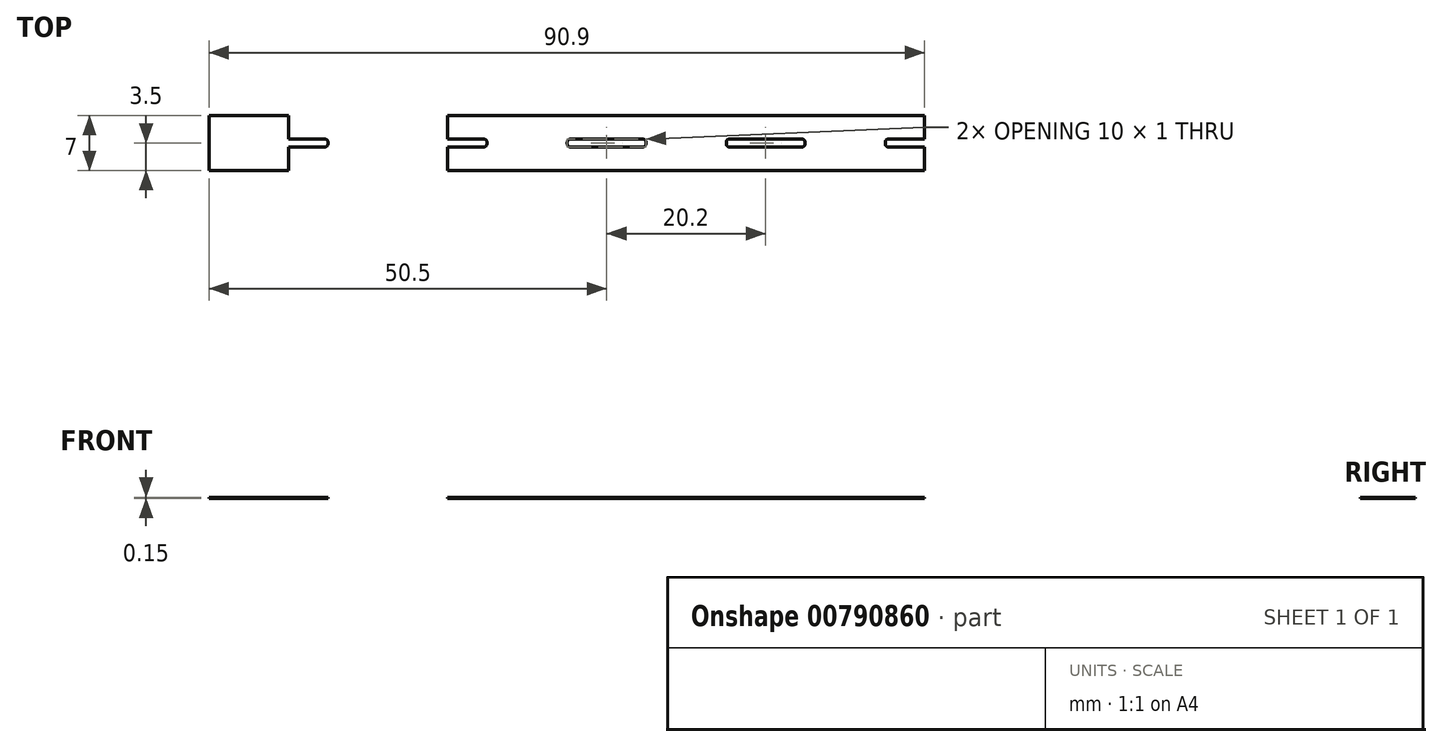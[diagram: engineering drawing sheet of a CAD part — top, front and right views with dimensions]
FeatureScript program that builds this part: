
annotation { "Feature Type Name" : "Feature", "Feature Type Description" : "" }
export const myFeature = defineFeature(function(context is Context, id is Id, definition is map)
    precondition{}
    {
        {
            var Q0;
            Q0=qCreatedBy(makeId("Top.planeOp"),FACE);
            var sketch = newSketch(context, id + "F0", { "sketchPlane" : qUnion([Q0])});
            skPoint(sketch, "E0.middle", {"position": v(0, 0) * mm});
            skLineSegment(sketch, "E1.bottom", {"start": v(-5.5, -0.5) * mm, "end": v(-10.1, -0.5) * mm});
            skLineSegment(sketch, "E1.top", {"start": v(-5.5, 0.5) * mm, "end": v(-10.1, 0.5) * mm});
            skLineSegment(sketch, "E1.left", {"start": v(-5.1, -0.1) * mm, "end": v(-5.1, 0.1) * mm});
            skLineSegment(sketch, "E1.right", {"start": v(-15.1, -0.1) * mm, "end": v(-15.1, 0.1) * mm});
            skPoint(sketch, "E1.middle", {"position": v(-10.1, 0) * mm});
            skPoint(sketch, "E2.visualSharp", {"position": v(-5.1, 0.5) * mm});
            skArc(sketch, "E2.filletArc", {"start": v(-5.1, 0.1) * mm, "mid": v(-5.22, 0.38) * mm, "end": v(-5.5, 0.5) * mm});
            skPoint(sketch, "E3.visualSharp", {"position": v(-5.1, -0.5) * mm});
            skArc(sketch, "E3.filletArc", {"start": v(-5.5, -0.5) * mm, "mid": v(-5.22, -0.38) * mm, "end": v(-5.1, -0.1) * mm});
            skPoint(sketch, "E4.visualSharp", {"position": v(-15.1, 0.5) * mm});
            skArc(sketch, "E4.filletArc", {"start": v(-14.7, 0.5) * mm, "mid": v(-14.98, 0.38) * mm, "end": v(-15.1, 0.1) * mm});
            skPoint(sketch, "E5.visualSharp", {"position": v(-15.1, -0.5) * mm});
            skArc(sketch, "E5.filletArc", {"start": v(-15.1, -0.1) * mm, "mid": v(-14.98, -0.38) * mm, "end": v(-14.7, -0.5) * mm});
            skLineSegment(sketch, "E6", {"start": v(0, 3.5) * mm, "end": v(-10.1, 3.5) * mm});
            skPoint(sketch, "E6.endSnap0", {"position": v(-10.1, 0.5) * mm});
            skLineSegment(sketch, "E7", {"start": v(-10.1, 3.5) * mm, "end": v(-10.1, 0.5) * mm});
            skLineSegment(sketch, "E8.MirrorCS", {"start": v(0, -3.5) * mm, "end": v(-10.1, -3.5) * mm});
            skLineSegment(sketch, "E9.MirrorCS", {"start": v(-10.1, -3.5) * mm, "end": v(-10.1, -0.5) * mm});
            skLineSegment(sketch, "E10.MirrorCS", {"start": v(0, 3.5) * mm, "end": v(10.1, 3.5) * mm});
            skLineSegment(sketch, "E11.MirrorCS", {"start": v(0, -3.5) * mm, "end": v(10.1, -3.5) * mm});
            skLineSegment(sketch, "E12.MirrorCS", {"start": v(5.1, -0.1) * mm, "end": v(5.1, 0.1) * mm});
            skArc(sketch, "E13.MirrorCS", {"start": v(5.1, 0.1) * mm, "mid": v(5.22, 0.38) * mm, "end": v(5.5, 0.5) * mm});
            skArc(sketch, "E14.MirrorCS", {"start": v(15.1, -0.1) * mm, "mid": v(14.98, -0.38) * mm, "end": v(14.7, -0.5) * mm});
            skLineSegment(sketch, "E15.MirrorCS", {"start": v(15.1, -0.1) * mm, "end": v(15.1, 0.1) * mm});
            skArc(sketch, "E16.MirrorCS", {"start": v(14.7, 0.5) * mm, "mid": v(14.98, 0.38) * mm, "end": v(15.1, 0.1) * mm});
            skArc(sketch, "E17.MirrorCS", {"start": v(5.5, -0.5) * mm, "mid": v(5.22, -0.38) * mm, "end": v(5.1, -0.1) * mm});
            skPoint(sketch, "E18.MirrorP", {"position": v(15.1, 0.5) * mm});
            skLineSegment(sketch, "E19.MirrorCS", {"start": v(5.5, 0.5) * mm, "end": v(14.7, 0.5) * mm});
            skLineSegment(sketch, "E20.MirrorCS", {"start": v(5.5, -0.5) * mm, "end": v(14.7, -0.5) * mm});
            skPoint(sketch, "E21.MirrorP", {"position": v(10.1, 0.5) * mm});
            skPoint(sketch, "E22.MirrorP", {"position": v(5.1, 0.5) * mm});
            skPoint(sketch, "E23.MirrorP", {"position": v(15.1, -0.5) * mm});
            skPoint(sketch, "E24.MirrorP", {"position": v(5.1, -0.5) * mm});
            skPoint(sketch, "E25.MirrorP", {"position": v(10.1, 0) * mm});
            skLineSegment(sketch, "E26.MirrorCS", {"start": v(10.1, 3.5) * mm, "end": v(10.1, 0.5) * mm});
            skLineSegment(sketch, "E27.MirrorCS", {"start": v(10.1, -3.5) * mm, "end": v(10.1, -0.5) * mm});
            skPoint(sketch, "E28.1.0.0", {"position": v(25.3, 0.5) * mm});
            skLineSegment(sketch, "E28.1.0.1", {"start": v(20.2, 3.5) * mm, "end": v(30.3, 3.5) * mm});
            skLineSegment(sketch, "E28.1.0.2", {"start": v(25.7, -0.5) * mm, "end": v(34.9, -0.5) * mm});
            skPoint(sketch, "E28.1.0.3", {"position": v(20.2, 0) * mm});
            skLineSegment(sketch, "E28.1.0.4", {"start": v(20.2, -3.5) * mm, "end": v(30.3, -3.5) * mm});
            skPoint(sketch, "E28.1.0.5", {"position": v(30.3, 0.5) * mm});
            skPoint(sketch, "E28.1.0.6", {"position": v(30.3, 0) * mm});
            skPoint(sketch, "E28.1.0.7", {"position": v(35.3, -0.5) * mm});
            skPoint(sketch, "E28.1.0.8", {"position": v(25.3, -0.5) * mm});
            skLineSegment(sketch, "E28.1.0.9", {"start": v(20.2, -3.5) * mm, "end": v(10.1, -3.5) * mm});
            skLineSegment(sketch, "E28.1.0.10", {"start": v(25.7, 0.5) * mm, "end": v(34.9, 0.5) * mm});
            skLineSegment(sketch, "E28.1.0.11", {"start": v(20.2, 3.5) * mm, "end": v(10.1, 3.5) * mm});
            skLineSegment(sketch, "E28.1.0.12", {"start": v(30.3, 3.5) * mm, "end": v(30.3, 0.5) * mm});
            skLineSegment(sketch, "E28.1.0.13", {"start": v(30.3, -3.5) * mm, "end": v(30.3, -0.5) * mm});
            skPoint(sketch, "E28.1.0.14", {"position": v(35.3, 0.5) * mm});
            skArc(sketch, "E28.1.0.15", {"start": v(34.9, 0.5) * mm, "mid": v(35.18, 0.38) * mm, "end": v(35.3, 0.1) * mm});
            skArc(sketch, "E28.1.0.16", {"start": v(25.7, -0.5) * mm, "mid": v(25.42, -0.38) * mm, "end": v(25.3, -0.1) * mm});
            skArc(sketch, "E28.1.0.17", {"start": v(35.3, -0.1) * mm, "mid": v(35.18, -0.38) * mm, "end": v(34.9, -0.5) * mm});
            skArc(sketch, "E28.1.0.18", {"start": v(25.3, 0.1) * mm, "mid": v(25.42, 0.38) * mm, "end": v(25.7, 0.5) * mm});
            skLineSegment(sketch, "E28.1.0.19", {"start": v(25.3, -0.1) * mm, "end": v(25.3, 0.1) * mm});
            skLineSegment(sketch, "E28.1.0.20", {"start": v(35.3, -0.1) * mm, "end": v(35.3, 0.1) * mm});
            skPoint(sketch, "E28.2.0.0", {"position": v(45.5, 0.5) * mm});
            skLineSegment(sketch, "E28.2.0.1", {"start": v(40.4, 3.5) * mm, "end": v(50.5, 3.5) * mm});
            skLineSegment(sketch, "E28.2.0.2", {"start": v(45.9, -0.5) * mm, "end": v(55.1, -0.5) * mm});
            skPoint(sketch, "E28.2.0.3", {"position": v(40.4, 0) * mm});
            skLineSegment(sketch, "E28.2.0.4", {"start": v(40.4, -3.5) * mm, "end": v(50.5, -3.5) * mm});
            skPoint(sketch, "E28.2.0.5", {"position": v(50.5, 0.5) * mm});
            skPoint(sketch, "E28.2.0.6", {"position": v(50.5, 0) * mm});
            skPoint(sketch, "E28.2.0.7", {"position": v(55.5, -0.5) * mm});
            skPoint(sketch, "E28.2.0.8", {"position": v(45.5, -0.5) * mm});
            skLineSegment(sketch, "E28.2.0.9", {"start": v(40.4, -3.5) * mm, "end": v(30.3, -3.5) * mm});
            skLineSegment(sketch, "E28.2.0.10", {"start": v(45.9, 0.5) * mm, "end": v(55.1, 0.5) * mm});
            skLineSegment(sketch, "E28.2.0.11", {"start": v(40.4, 3.5) * mm, "end": v(30.3, 3.5) * mm});
            skLineSegment(sketch, "E28.2.0.12", {"start": v(50.5, 3.5) * mm, "end": v(50.5, 0.5) * mm});
            skLineSegment(sketch, "E28.2.0.13", {"start": v(50.5, -3.5) * mm, "end": v(50.5, -0.5) * mm});
            skPoint(sketch, "E28.2.0.14", {"position": v(55.5, 0.5) * mm});
            skArc(sketch, "E28.2.0.15", {"start": v(55.1, 0.5) * mm, "mid": v(55.38, 0.38) * mm, "end": v(55.5, 0.1) * mm});
            skArc(sketch, "E28.2.0.16", {"start": v(45.9, -0.5) * mm, "mid": v(45.62, -0.38) * mm, "end": v(45.5, -0.1) * mm});
            skArc(sketch, "E28.2.0.17", {"start": v(55.5, -0.1) * mm, "mid": v(55.38, -0.38) * mm, "end": v(55.1, -0.5) * mm});
            skArc(sketch, "E28.2.0.18", {"start": v(45.5, 0.1) * mm, "mid": v(45.62, 0.38) * mm, "end": v(45.9, 0.5) * mm});
            skLineSegment(sketch, "E28.2.0.19", {"start": v(45.5, -0.1) * mm, "end": v(45.5, 0.1) * mm});
            skLineSegment(sketch, "E28.2.0.20", {"start": v(55.5, -0.1) * mm, "end": v(55.5, 0.1) * mm});
            skPoint(sketch, "E28.3.0.0", {"position": v(65.7, 0.5) * mm});
            skLineSegment(sketch, "E28.3.0.1", {"start": v(60.6, 3.5) * mm, "end": v(70.7, 3.5) * mm});
            skLineSegment(sketch, "E28.3.0.2", {"start": v(66.1, -0.5) * mm, "end": v(75.3, -0.5) * mm});
            skPoint(sketch, "E28.3.0.3", {"position": v(60.6, 0) * mm});
            skLineSegment(sketch, "E28.3.0.4", {"start": v(60.6, -3.5) * mm, "end": v(70.7, -3.5) * mm});
            skPoint(sketch, "E28.3.0.5", {"position": v(70.7, 0.5) * mm});
            skPoint(sketch, "E28.3.0.6", {"position": v(70.7, 0) * mm});
            skPoint(sketch, "E28.3.0.7", {"position": v(75.7, -0.5) * mm});
            skPoint(sketch, "E28.3.0.8", {"position": v(65.7, -0.5) * mm});
            skLineSegment(sketch, "E28.3.0.9", {"start": v(60.6, -3.5) * mm, "end": v(50.5, -3.5) * mm});
            skLineSegment(sketch, "E28.3.0.10", {"start": v(66.1, 0.5) * mm, "end": v(75.3, 0.5) * mm});
            skLineSegment(sketch, "E28.3.0.11", {"start": v(60.6, 3.5) * mm, "end": v(50.5, 3.5) * mm});
            skLineSegment(sketch, "E28.3.0.12", {"start": v(70.7, 3.5) * mm, "end": v(70.7, 0.5) * mm});
            skLineSegment(sketch, "E28.3.0.13", {"start": v(70.7, -3.5) * mm, "end": v(70.7, -0.5) * mm});
            skPoint(sketch, "E28.3.0.14", {"position": v(75.7, 0.5) * mm});
            skArc(sketch, "E28.3.0.15", {"start": v(75.3, 0.5) * mm, "mid": v(75.58, 0.38) * mm, "end": v(75.7, 0.1) * mm});
            skArc(sketch, "E28.3.0.16", {"start": v(66.1, -0.5) * mm, "mid": v(65.82, -0.38) * mm, "end": v(65.7, -0.1) * mm});
            skArc(sketch, "E28.3.0.17", {"start": v(75.7, -0.1) * mm, "mid": v(75.58, -0.38) * mm, "end": v(75.3, -0.5) * mm});
            skArc(sketch, "E28.3.0.18", {"start": v(65.7, 0.1) * mm, "mid": v(65.82, 0.38) * mm, "end": v(66.1, 0.5) * mm});
            skLineSegment(sketch, "E28.3.0.19", {"start": v(65.7, -0.1) * mm, "end": v(65.7, 0.1) * mm});
            skLineSegment(sketch, "E28.3.0.20", {"start": v(75.7, -0.1) * mm, "end": v(75.7, 0.1) * mm});
            skPoint(sketch, "E28.4.0.0", {"position": v(85.9, 0.5) * mm});
            skLineSegment(sketch, "E28.4.0.1", {"start": v(80.8, 3.5) * mm, "end": v(90.9, 3.5) * mm});
            skLineSegment(sketch, "E28.4.0.2", {"start": v(86.3, -0.5) * mm, "end": v(95.5, -0.5) * mm});
            skPoint(sketch, "E28.4.0.3", {"position": v(80.8, 0) * mm});
            skLineSegment(sketch, "E28.4.0.4", {"start": v(80.8, -3.5) * mm, "end": v(90.9, -3.5) * mm});
            skPoint(sketch, "E28.4.0.5", {"position": v(90.9, 0.5) * mm});
            skPoint(sketch, "E28.4.0.6", {"position": v(90.9, 0) * mm});
            skPoint(sketch, "E28.4.0.7", {"position": v(95.9, -0.5) * mm});
            skPoint(sketch, "E28.4.0.8", {"position": v(85.9, -0.5) * mm});
            skLineSegment(sketch, "E28.4.0.9", {"start": v(80.8, -3.5) * mm, "end": v(70.7, -3.5) * mm});
            skLineSegment(sketch, "E28.4.0.10", {"start": v(86.3, 0.5) * mm, "end": v(95.5, 0.5) * mm});
            skLineSegment(sketch, "E28.4.0.11", {"start": v(80.8, 3.5) * mm, "end": v(70.7, 3.5) * mm});
            skLineSegment(sketch, "E28.4.0.12", {"start": v(90.9, 3.5) * mm, "end": v(90.9, 0.5) * mm});
            skLineSegment(sketch, "E28.4.0.13", {"start": v(90.9, -3.5) * mm, "end": v(90.9, -0.5) * mm});
            skPoint(sketch, "E28.4.0.14", {"position": v(95.9, 0.5) * mm});
            skArc(sketch, "E28.4.0.15", {"start": v(95.5, 0.5) * mm, "mid": v(95.78, 0.38) * mm, "end": v(95.9, 0.1) * mm});
            skArc(sketch, "E28.4.0.16", {"start": v(86.3, -0.5) * mm, "mid": v(86.02, -0.38) * mm, "end": v(85.9, -0.1) * mm});
            skArc(sketch, "E28.4.0.17", {"start": v(95.9, -0.1) * mm, "mid": v(95.78, -0.38) * mm, "end": v(95.5, -0.5) * mm});
            skArc(sketch, "E28.4.0.18", {"start": v(85.9, 0.1) * mm, "mid": v(86.02, 0.38) * mm, "end": v(86.3, 0.5) * mm});
            skLineSegment(sketch, "E28.4.0.19", {"start": v(85.9, -0.1) * mm, "end": v(85.9, 0.1) * mm});
            skLineSegment(sketch, "E28.4.0.20", {"start": v(95.9, -0.1) * mm, "end": v(95.9, 0.1) * mm});
            skLineSegment(sketch, "E28.direction1", {"start": v(-10.1, -3.5) * mm, "end": v(10.1, -3.5) * mm, "construction": true});
            skLineSegment(sketch, "E29", {"start": v(0, 3.5) * mm, "end": v(0, -3.5) * mm});
            skSolve(sketch);
        }
        {
            var Q0;
            {var subQ8=sQuery(id+"F0.wireOp",EDGE,"E28.3.0.12");Q0=makeQuery(id+"F0.imprint","IMPRINT",FACE,{"disambiguationData":[TD([[makeQuery(id+"F0.imprint","IMPRINT",EDGE,{"derivedFrom":subQ8}),1.0]])]});}
            var Q1;
            {var subQ3=sQuery(id+"F0.wireOp",EDGE,"E14.MirrorCS");Q1=makeQuery(id+"F0.imprint","IMPRINT",FACE,{"disambiguationData":[TD([[makeQuery(id+"F0.imprint","IMPRINT",EDGE,{"derivedFrom":subQ3}),1.0]])]});}
            var Q2;
            {var subQ8=sQuery(id+"F0.wireOp",EDGE,"E28.1.0.12");Q2=makeQuery(id+"F0.imprint","IMPRINT",FACE,{"disambiguationData":[TD([[makeQuery(id+"F0.imprint","IMPRINT",EDGE,{"derivedFrom":subQ8}),1.0]])]});}
            var Q3;
            {var subQ8=sQuery(id+"F0.wireOp",EDGE,"E28.2.0.12");Q3=makeQuery(id+"F0.imprint","IMPRINT",FACE,{"disambiguationData":[TD([[makeQuery(id+"F0.imprint","IMPRINT",EDGE,{"derivedFrom":subQ8}),1.0]])]});}
            var Q4;
            Q4=makeQuery(id+"F0.imprint","IMPRINT",FACE,{"disambiguationData":[TD([[makeQuery(id+"F0.imprint","IMPRINT",EDGE,{"derivedFrom":sQuery(id+"F0.wireOp",EDGE,"E10.MirrorCS")}),-1.0]])]});
            extrude(context, id + "F1", {"entities" : qUnion([Q0, Q1, Q2, Q3, Q4]), "depth" : 0.15 * mm, "offsetDistance" : 25 * mm});
        }
    });
